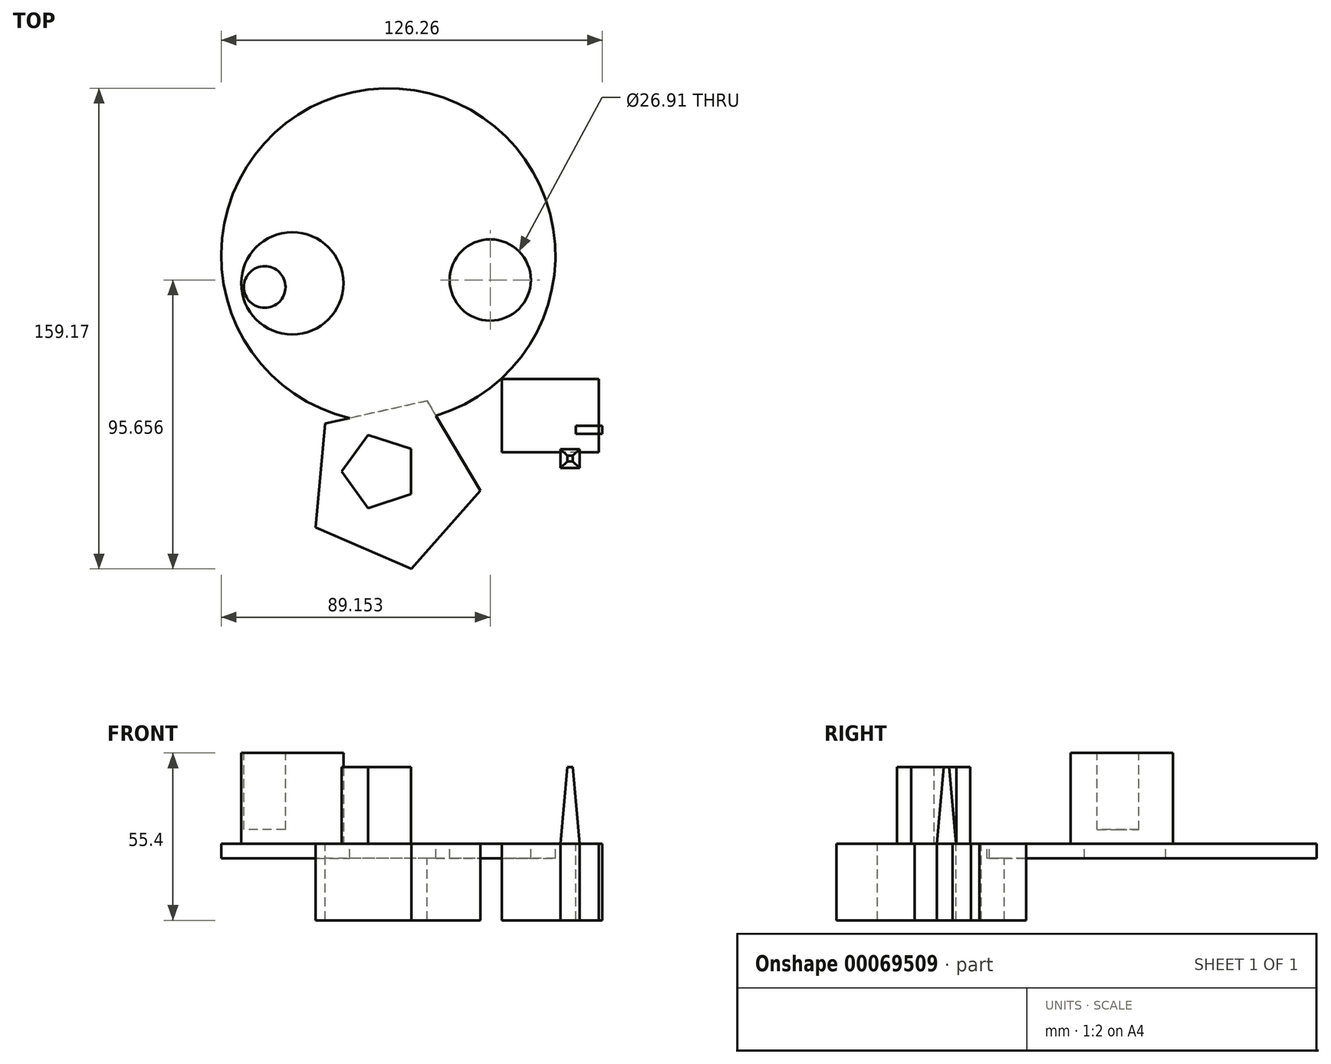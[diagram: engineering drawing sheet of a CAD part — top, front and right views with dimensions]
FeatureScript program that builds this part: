
annotation { "Feature Type Name" : "Feature", "Feature Type Description" : "" }
export const myFeature = defineFeature(function(context is Context, id is Id, definition is map)
    precondition{}
    {
        {
            var Q0;
            Q0=qCreatedBy(makeId("Top.planeOp"),FACE);
            var sketch = newSketch(context, id + "F0", { "sketchPlane" : qUnion([Q0])});
            skArc(sketch, "E0", {"start": v(0, 0) * mm, "mid": v(39.18, 34.63) * mm, "end": v(-12.2, 44.29) * mm});
            skCircle(sketch, "E1.cCircle", {"center": v(-23.83, -25.71) * mm, "radius": 23.79 * mm, "construction": true});
            skLineSegment(sketch, "E1.0", {"start": v(5.44, -28.45) * mm, "end": v(-17.39, -54.4) * mm});
            skLineSegment(sketch, "E1.1", {"start": v(-17.39, -54.4) * mm, "end": v(-49.12, -40.71) * mm});
            skLineSegment(sketch, "E1.2", {"start": v(-49.12, -40.71) * mm, "end": v(-45.9, -6.3) * mm});
            skLineSegment(sketch, "E1.3", {"start": v(-45.9, -6.3) * mm, "end": v(-12.19, 1.28) * mm});
            skLineSegment(sketch, "E1.4", {"start": v(-12.19, 1.28) * mm, "end": v(5.44, -28.45) * mm});
            skPoint(sketch, "E1.0.midPoint", {"position": v(-5.97, -41.42) * mm});
            skSolve(sketch);
        }
        {
            var Q0;
            Q0=makeQuery(id+"F0.imprint","IMPRINT",FACE,{"disambiguationData":[TD([[makeQuery(id+"F0.imprint","IMPRINT",EDGE,{"derivedFrom":sQuery(id+"F0.wireOp",EDGE,"E1.0")}),-1.0]])]});
            extrude(context, id + "F1", {"entities" : qUnion([Q0]), "oppositeDirection" : true, "depth" : 25.4 * mm});
        }
        {
            var Q0;
            Q0=qCreatedBy(makeId("Top.planeOp"),FACE);
            var sketch = newSketch(context, id + "F2", { "sketchPlane" : qUnion([Q0])});
            skArc(sketch, "E2", {"start": v(63.03, -29.84) * mm, "mid": v(43.75, 28.3) * mm, "end": v(46.44, -32.9) * mm});
            skArc(sketch, "E3", {"start": v(37.17, -30.53) * mm, "mid": v(48.77, -2.78) * mm, "end": v(22.9, -18.14) * mm});
            skSolve(sketch);
        }
        {
            var Q0;
            Q0 = qSketchRegion(id + "F2", true);
            extrude(context, id + "F3", {"entities" : qUnion([Q0]), "oppositeDirection" : true, "depth" : 25.4 * mm});
        }
        {
            var Q0;
            Q0=qCreatedBy(makeId("Top.planeOp"),FACE);
            var sketch = newSketch(context, id + "F4", { "sketchPlane" : qUnion([Q0])});
            skCircle(sketch, "E4", {"center": v(-25.01, 49.4) * mm, "radius": 55.37 * mm});
            skSolve(sketch);
        }
        {
            var Q0;
            Q0 = qSketchRegion(id + "F4", true);
            extrude(context, id + "F5", {"entities" : qUnion([Q0]), "operationType" : NewBodyOperationType.ADD, "oppositeDirection" : true, "depth" : 4.8 * mm});
        }
        {
            var Q0;
            Q0=makeQuery(id+"F5.boolean.opBoolean","MERGE",FACE,{"derivedFrom":[makeQuery(id+"F1.opExtrude","CAP_FACE",FACE,{"disambiguationData":[OSD([sQuery(id+"F0.wireOp",EDGE,"E1.0"),sQuery(id+"F0.wireOp",EDGE,"E1.1"),sQuery(id+"F0.wireOp",EDGE,"E1.2"),sQuery(id+"F0.wireOp",EDGE,"E1.3"),sQuery(id+"F0.wireOp",EDGE,"E1.4")])],"isStart":true}),makeQuery(id+"F5.opExtrude","CAP_FACE",FACE,{"disambiguationData":[OSD([sQuery(id+"F4.wireOp",EDGE,"E4")])],"isStart":true})]});
            var sketch = newSketch(context, id + "F6", { "sketchPlane" : qUnion([Q0])});
            skCircle(sketch, "E5", {"center": v(-56.83, 40.16) * mm, "radius": 16.94 * mm});
            skSolve(sketch);
        }
        {
            var Q0;
            Q0=makeQuery(id+"F6.imprint","IMPRINT",FACE,{"disambiguationData":[TD([[makeQuery(id+"F6.imprint","IMPRINT",EDGE,{"derivedFrom":sQuery(id+"F6.wireOp",EDGE,"E5")}),1.0]])]});
            extrude(context, id + "F7", {"entities" : qUnion([Q0]), "operationType" : NewBodyOperationType.ADD, "depth" : 30 * mm});
        }
        {
            var Q0;
            Q0=makeQuery(id+"F3.opExtrude","CAP_FACE",FACE,{"disambiguationData":[OSD([sQuery(id+"F2.wireOp",EDGE,"E2"),sQuery(id+"F2.wireOp",EDGE,"E3")])],"isStart":true});
            var sketch = newSketch(context, id + "F8", { "sketchPlane" : qUnion([Q0])});
            skLineSegment(sketch, "E6.bottom", {"start": v(32.08, -21.03) * mm, "end": v(38.38, -21.03) * mm});
            skLineSegment(sketch, "E6.top", {"start": v(32.08, -14.73) * mm, "end": v(38.38, -14.73) * mm});
            skLineSegment(sketch, "E6.left", {"start": v(32.08, -21.03) * mm, "end": v(32.08, -14.73) * mm});
            skLineSegment(sketch, "E6.right", {"start": v(38.38, -21.03) * mm, "end": v(38.38, -14.73) * mm});
            skSolve(sketch);
        }
        {
            var Q0;
            Q0=makeQuery(id+"F8.imprint","IMPRINT",FACE,{"disambiguationData":[TD([[makeQuery(id+"F8.imprint","IMPRINT",EDGE,{"derivedFrom":sQuery(id+"F8.wireOp",EDGE,"E6.bottom")}),1.0]])]});
            extrude(context, id + "F9", {"entities" : qUnion([Q0]), "operationType" : NewBodyOperationType.ADD, "depth" : 25.4 * mm, "hasDraft" : true, "draftAngle" : 5 * degree, "draftPullDirection" : true});
        }
        {
            var Q0;
            Q0=makeQuery(id+"F5.boolean.opBoolean","MERGE",FACE,{"derivedFrom":[makeQuery(id+"F1.opExtrude","CAP_FACE",FACE,{"disambiguationData":[OSD([sQuery(id+"F0.wireOp",EDGE,"E1.0"),sQuery(id+"F0.wireOp",EDGE,"E1.1"),sQuery(id+"F0.wireOp",EDGE,"E1.2"),sQuery(id+"F0.wireOp",EDGE,"E1.3"),sQuery(id+"F0.wireOp",EDGE,"E1.4")])],"isStart":true}),makeQuery(id+"F5.opExtrude","CAP_FACE",FACE,{"disambiguationData":[OSD([sQuery(id+"F4.wireOp",EDGE,"E4")])],"isStart":true})]});
            var sketch = newSketch(context, id + "F10", { "sketchPlane" : qUnion([Q0])});
            skCircle(sketch, "E7.cCircle", {"center": v(-27.78, -22.15) * mm, "radius": 10.32 * mm, "construction": true});
            skLineSegment(sketch, "E7.0", {"start": v(-17.46, -14.65) * mm, "end": v(-17.46, -29.65) * mm});
            skLineSegment(sketch, "E7.1", {"start": v(-17.46, -29.65) * mm, "end": v(-31.72, -34.28) * mm});
            skLineSegment(sketch, "E7.2", {"start": v(-31.72, -34.28) * mm, "end": v(-40.53, -22.15) * mm});
            skLineSegment(sketch, "E7.3", {"start": v(-40.53, -22.15) * mm, "end": v(-31.72, -10.02) * mm});
            skLineSegment(sketch, "E7.4", {"start": v(-31.72, -10.02) * mm, "end": v(-17.46, -14.65) * mm});
            skPoint(sketch, "E7.0.midPoint", {"position": v(-17.46, -22.15) * mm});
            skSolve(sketch);
        }
        {
            var Q0;
            Q0=makeQuery(id+"F10.imprint","IMPRINT",FACE,{"disambiguationData":[TD([[makeQuery(id+"F10.imprint","IMPRINT",EDGE,{"derivedFrom":sQuery(id+"F10.wireOp",EDGE,"E7.0")}),-1.0]])]});
            extrude(context, id + "F11", {"entities" : qUnion([Q0]), "operationType" : NewBodyOperationType.ADD, "depth" : 25.4 * mm});
        }
        {
            var Q0;
            Q0=makeQuery(id+"F5.boolean.opBoolean","MERGE",FACE,{"derivedFrom":[makeQuery(id+"F1.opExtrude","CAP_FACE",FACE,{"disambiguationData":[OSD([sQuery(id+"F0.wireOp",EDGE,"E1.0"),sQuery(id+"F0.wireOp",EDGE,"E1.1"),sQuery(id+"F0.wireOp",EDGE,"E1.2"),sQuery(id+"F0.wireOp",EDGE,"E1.3"),sQuery(id+"F0.wireOp",EDGE,"E1.4")])],"isStart":true}),makeQuery(id+"F5.opExtrude","CAP_FACE",FACE,{"disambiguationData":[OSD([sQuery(id+"F4.wireOp",EDGE,"E4")])],"isStart":true})]});
            var sketch = newSketch(context, id + "F12", { "sketchPlane" : qUnion([Q0])});
            skSolve(sketch);
        }
        {
            var Q0;
            Q0=makeQuery(id+"F12.imprint","IMPRINT",FACE,{"disambiguationData":[TD([[makeQuery(id+"F12.imprint","IMPRINT",EDGE,{"derivedFrom":makeQuery(id+"F1.opExtrude","CAP_EDGE",EDGE,{"disambiguationData":[OSD([sQuery(id+"F0.wireOp",EDGE,"E1.0")])],"isStart":true})}),-1.0]])]});
            var sketch = newSketch(context, id + "F13", { "sketchPlane" : qUnion([Q0])});
            skCircle(sketch, "E8", {"center": v(8.77, 41.26) * mm, "radius": 13.46 * mm});
            skSolve(sketch);
        }
        {
            var Q0;
            Q0=makeQuery(id+"F13.imprint","IMPRINT",FACE,{"disambiguationData":[TD([[makeQuery(id+"F13.imprint","IMPRINT",EDGE,{"derivedFrom":sQuery(id+"F13.wireOp",EDGE,"E8")}),1.0]])]});
            extrude(context, id + "F14", {"entities" : qUnion([Q0]), "operationType" : NewBodyOperationType.REMOVE, "oppositeDirection" : true, "depth" : 25.4 * mm});
        }
        {
            var Q0;
            Q0=makeQuery(id+"F7.opExtrude","CAP_FACE",FACE,{"disambiguationData":[OSD([sQuery(id+"F6.wireOp",EDGE,"E5")])],"isStart":false});
            var sketch = newSketch(context, id + "F15", { "sketchPlane" : qUnion([Q0])});
            skCircle(sketch, "E9", {"center": v(-65.96, 38.93) * mm, "radius": 6.9 * mm});
            skSolve(sketch);
        }
        {
            var Q0;
            Q0=makeQuery(id+"F15.imprint","IMPRINT",FACE,{"disambiguationData":[TD([[makeQuery(id+"F15.imprint","IMPRINT",EDGE,{"derivedFrom":sQuery(id+"F15.wireOp",EDGE,"E9")}),1.0]])]});
            extrude(context, id + "F16", {"entities" : qUnion([Q0]), "operationType" : NewBodyOperationType.REMOVE, "oppositeDirection" : true, "depth" : 25.4 * mm});
        }
        {
            var Q0;
            Q0=makeQuery(id+"F3.opExtrude","CAP_FACE",FACE,{"disambiguationData":[OSD([sQuery(id+"F2.wireOp",EDGE,"E2"),sQuery(id+"F2.wireOp",EDGE,"E3")])],"isStart":true});
            var sketch = newSketch(context, id + "F17", { "sketchPlane" : qUnion([Q0])});
            skLineSegment(sketch, "E10.bottom", {"start": v(45.88, -9.72) * mm, "end": v(37.17, -9.72) * mm});
            skLineSegment(sketch, "E10.top", {"start": v(45.88, -7.02) * mm, "end": v(37.17, -7.02) * mm});
            skLineSegment(sketch, "E10.left", {"start": v(45.88, -9.72) * mm, "end": v(45.88, -7.02) * mm});
            skLineSegment(sketch, "E10.right", {"start": v(37.17, -9.72) * mm, "end": v(37.17, -7.02) * mm});
            skSolve(sketch);
        }
        {
            var Q0;
            Q0=makeQuery(id+"F17.imprint","IMPRINT",FACE,{"disambiguationData":[TD([[makeQuery(id+"F17.imprint","IMPRINT",EDGE,{"derivedFrom":sQuery(id+"F17.wireOp",EDGE,"E10.bottom")}),1.0]])]});
            extrude(context, id + "F18", {"entities" : qUnion([Q0]), "operationType" : NewBodyOperationType.REMOVE, "oppositeDirection" : true, "depth" : 25.4 * mm});
        }
        {
            var Q0;
            Q0=qCreatedBy(makeId("Top.planeOp"),FACE);
            var sketch = newSketch(context, id + "F19", { "sketchPlane" : qUnion([Q0])});
            skLineSegment(sketch, "E11.bottom", {"start": v(44.72, -15.84) * mm, "end": v(12.57, -15.84) * mm});
            skLineSegment(sketch, "E11.top", {"start": v(44.72, 8.48) * mm, "end": v(12.57, 8.48) * mm});
            skLineSegment(sketch, "E11.left", {"start": v(44.72, -15.84) * mm, "end": v(44.72, 8.48) * mm});
            skLineSegment(sketch, "E11.right", {"start": v(12.57, -15.84) * mm, "end": v(12.57, 8.48) * mm});
            skSolve(sketch);
        }
        {
            var Q0;
            Q0=makeQuery(id+"F19.imprint","IMPRINT",FACE,{"disambiguationData":[TD([[makeQuery(id+"F19.imprint","IMPRINT",EDGE,{"derivedFrom":sQuery(id+"F19.wireOp",EDGE,"E11.bottom")}),-1.0]])]});
            extrude(context, id + "F20", {"entities" : qUnion([Q0]), "oppositeDirection" : true, "depth" : 25.4 * mm});
        }
    });
